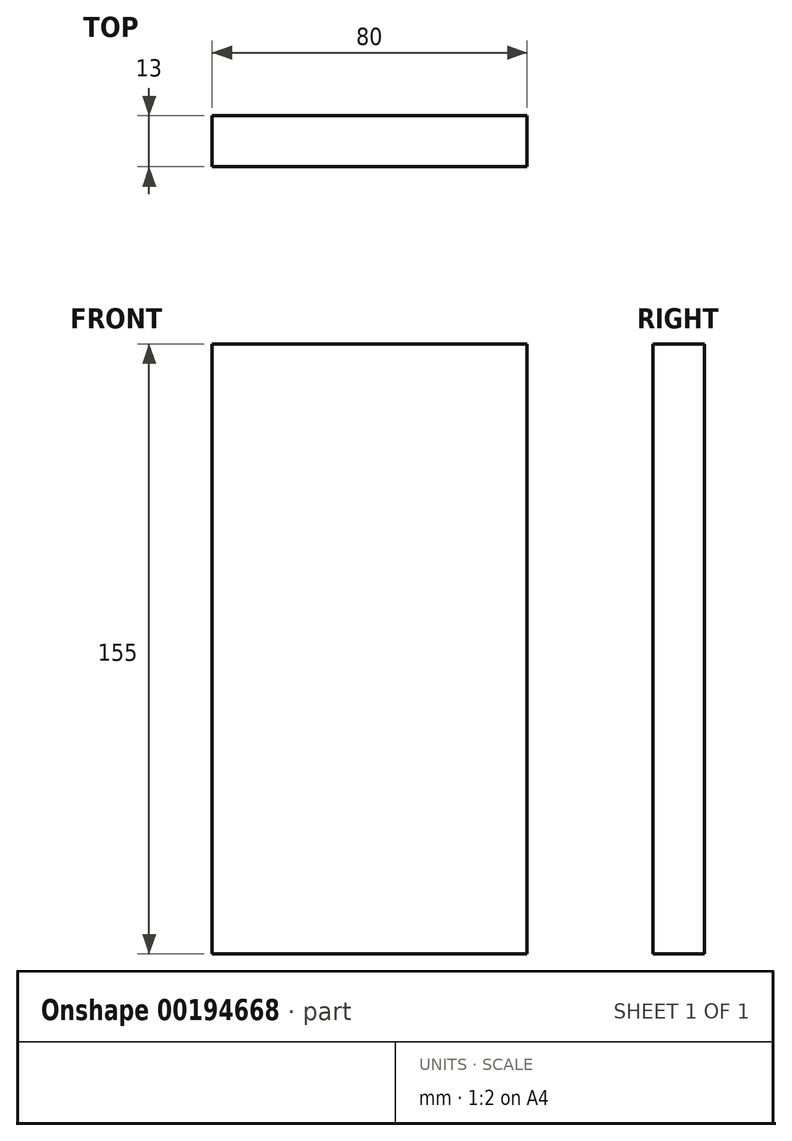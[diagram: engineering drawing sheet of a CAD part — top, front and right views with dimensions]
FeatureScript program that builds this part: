
annotation { "Feature Type Name" : "Feature", "Feature Type Description" : "" }
export const myFeature = defineFeature(function(context is Context, id is Id, definition is map)
    precondition{}
    {
        {
            var Q0;
            Q0=qCreatedBy(makeId("Top.planeOp"),FACE);
            var sketch = newSketch(context, id + "F0", { "sketchPlane" : qUnion([Q0])});
            skLineSegment(sketch, "E0.bottom", {"start": v(40, 6.5) * mm, "end": v(-40, 6.5) * mm});
            skLineSegment(sketch, "E0.top", {"start": v(40, -6.5) * mm, "end": v(-40, -6.5) * mm});
            skLineSegment(sketch, "E0.left", {"start": v(40, 6.5) * mm, "end": v(40, -6.5) * mm});
            skLineSegment(sketch, "E0.right", {"start": v(-40, 6.5) * mm, "end": v(-40, -6.5) * mm});
            skPoint(sketch, "E0.middle", {"position": v(0, 0) * mm});
            skLineSegment(sketch, "E1", {"start": v(0, 6.5) * mm, "end": v(0, -6.5) * mm});
            skSolve(sketch);
        }
        {
            var Q0;
            Q0=makeQuery(id+"F0.imprint","IMPRINT",FACE,{"disambiguationData":[TD([[makeQuery(id+"F0.imprint","IMPRINT",EDGE,{"derivedFrom":sQuery(id+"F0.wireOp",EDGE,"E0.bottom")}),1.0]])]});
            extrude(context, id + "F1", {"entities" : qUnion([Q0]), "depth" : 155 * mm});
        }
    });
